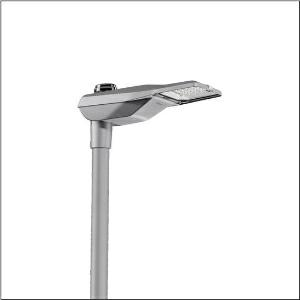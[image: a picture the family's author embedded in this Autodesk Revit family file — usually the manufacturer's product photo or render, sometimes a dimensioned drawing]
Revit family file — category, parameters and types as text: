
# Revit family: streetlight_sl_21_micro___st1_5a_5xe5p47n08cb_4c70
name_source: partatom
category: Lighting Fixtures
units: mm (PartAtom-declared; Revit-internal decimal feet)

## family parameters
Cut with Voids When Loaded = No
Host = Face
Light Source = No
Part Type = Normal
Room Calculation Point = No
Round Connector Dimension = Use Diameter
Shared = No

## types (1)
- --- (1 x LED, 2340 lm, 15.8 W, 4000K)
    Apparent Load = 16 VA
    CIE Flux Codes = 22 53 95 100 100
    Color Rendering = 70
    Color Temperature = 4000K
    Default Elevation = 1800 mm
    Description = Streetlight SL 21 micro, mast luminaire, primary light control with lens, of PMMA, primary optical cover: cover, of toughened safety glass, transparent, light distribution: ST1.5a, light emission: direct distribution, primary light characteristic: asymmetric, installation type: post-top, LED, 3G 1.5mm², High Power LED, rated luminous flux: 2.340lm, luminous efficacy: 148lm/W, light colour: 740, colour temperature: 4000K, control: overheat protection, presetting dimming linear, constant luminous flux control, time-dependent luminous flux control, flexible luminous flux parameterisation, mains connection: 230..240V, AC, 50/60Hz, connection cable pre-assembled, cable length: 6,5m, wiring characteristics: H07RN-F, start of lifetime: 16W, end of service life: 16W, reduction: 8W, luminaire housing, of diecast aluminium (EN AC-44300), powder-coated, Siteco® metallic grey (DB 702S), corrosivity category C5 mid according to DIN EN ISO 12944, multi-level sealing system, sealing non-destructively replaceable, inclination adjustable: 0°, 5°, 10°, 15°, length: 528mm, width: 235mm, height: 110mm, spigot size: 76/60mm (post-top), protection rating (complete): IP66, insulation class (complete): insulation class I (protective earthing), certification: CE, ENEC, ENEC+, VDE, impact resistance: IK09, permissible operating ambient temperature for outdoor applications: -40..+50°C, standard-compliant lighting for roads and squares, packaging unit: 1 piece

Light Distribution: ST1.5a
    Height = 110 mm
    Lamp = 1 x LED
    Lamp Light Flux = 2340 lm
    Lamp Power = 15.8 W
    Lamp count = 1
    Length = 528 mm
    Luminous efficacy = 148 lm/W
    Manufacturer = Siteco
    ModVariant = No
    Model = 5XE5P47N08CB
    Number of Poles = 1
    OnlyDefault = Yes
    Power Factor = 1
    Product Name = Streetlight SL 21 micro | ST1.5a
    Product group = mast luminaire | pylon top
    ProductGroupID = 6100
    Protection Class = Protection class I
    Protection Degree = IP 66
    RLX_Detail_Level = 1
    RLX_Emergency_Light_Flux = 0 lm
    RLX_Emergency_Type = 0
    RLX_Emergency_Type_DB = No
    RlxData = <blob elided: 102741 chars, md5=6da6351a>
    Socket = socket
    Standby Power = 0 W
    System Light Flux = 2340 lm
    System Power = 16 W
    Type Comments = factory setting: luminous flux: 100 % | dim-lin: 254 | 300 mA
    Type Image = l_1294375.jpg
    URL = http://relux.com
    VarID = @adj_083111
    Voltage = 0 V
    Weight = 0.00 kg
    Width = 235 mm

## geometry (parser evidence)
native form markers: Blend x4, Sweep x11
no freeform markers — native parametric forms only
